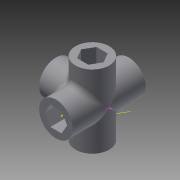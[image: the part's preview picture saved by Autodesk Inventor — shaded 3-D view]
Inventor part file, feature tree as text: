
AUTODESK INVENTOR PART (.ipt)
format: ipt  version: 2015 SP1 (Build 190203100, 203)  size: 421,376 bytes
history: native  units: mm
features: sketch x8, projected_geometry x8, extrude x7, other x5, pattern_circular x2, fillet x1
ambient origin geometry x8: Origin, YZ Plane, XZ Plane, XY Plane, X Axis, Y Axis, Z Axis, Center Point
bodies: Body1 (feature_tree)
feature tree (31):
  other  "Sólido1"
  extrude  "Extrusión1"  Depth=12.0mm
  extrude  "Extrusión2"  Depth=2.0mm TaperAngle=0.0deg
  other  "Eje de trabajo1"
  other  "Eje de trabajo2"
  pattern_circular  "Patrón circular3"  Count=4 Angle=360.0deg
  other  "Eje de trabajo6"
  pattern_circular  "Patrón circular5"  Count=2 Angle=90.0deg
  fillet  "Empalme4"  Radius=2.0mm
  extrude  "Extrusión13"  Depth=10.0mm TaperAngle=0.0deg
  extrude  "Extrusión14"  Depth=200.0mm TaperAngle=0.0deg
  extrude  "Extrusión15"  [1 undecoded]
  sketch  "Boceto17"
  extrude  "Extrusión18"  [1 undecoded]
  extrude  "Extrusión19"  [1 undecoded]
  sketch  "Boceto1"  dims[d0=8.0mm d1=12.0mm]
  sketch  "Boceto2"  dims[d2=7.0mm d3=0.0mm d4=6.0mm d5=0.0mm d19=40.0mm d20=360.0deg d41=20.0mm d42=90.0deg d44=2.0mm]
  other  "Punto de trabajo1"
  sketch  "Boceto14"  dims[d45=10.0mm d46=0.0mm d47=10.0mm d48=0.0mm]
  projected_geometry  "Contorno proyectado12"
  sketch  "Boceto15"  dims[d49=10.0mm d50=0.0mm d56=200.0mm d57=0.0mm]
  projected_geometry  "Contorno proyectado13"
  projected_geometry  "Contorno proyectado14"
  projected_geometry  "Contorno proyectado15"
  sketch  "Boceto16"  dims[d58=200.0mm d59=0.0mm]
  projected_geometry  "Contorno proyectado16"
  projected_geometry  "Contorno proyectado17"
  sketch  "Boceto22"
  projected_geometry  "Contorno proyectado22"
  sketch  "Boceto23"
  projected_geometry  "Contorno proyectado23"
note: 3 required parameter values undecoded (feature->parameter linkage not recoverable at this tier; creation-order binding heuristic only, values carry confidence <= 0.55)
